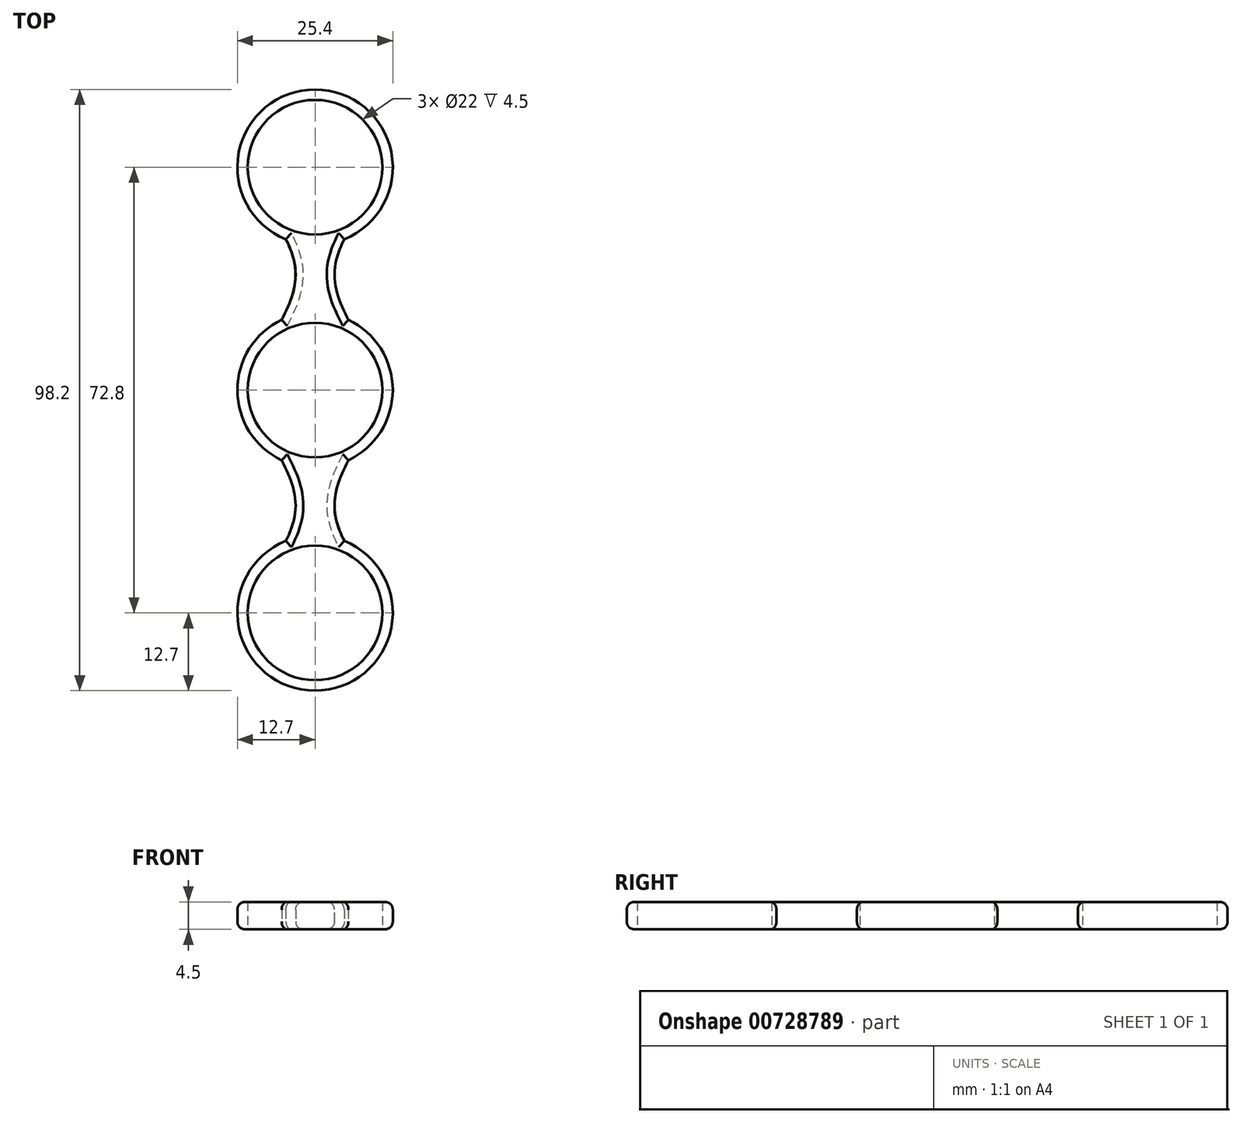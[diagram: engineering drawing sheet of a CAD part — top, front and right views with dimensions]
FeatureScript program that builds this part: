
annotation { "Feature Type Name" : "Feature", "Feature Type Description" : "" }
export const myFeature = defineFeature(function(context is Context, id is Id, definition is map)
    precondition{}
    {
        {
            var Q0;
            Q0=qCreatedBy(makeId("Top.planeOp"),FACE);
            var sketch = newSketch(context, id + "F0", { "sketchPlane" : qUnion([Q0])});
            skCircle(sketch, "E0", {"center": v(0, 0) * mm, "radius": 12.7 * mm});
            skCircle(sketch, "E1", {"center": v(0, 36.4) * mm, "radius": 11 * mm});
            skLineSegment(sketch, "E2", {"start": v(0, 25.4) * mm, "end": v(0, 12.7) * mm});
            skCircle(sketch, "E3", {"center": v(0, 0) * mm, "radius": 11 * mm});
            skCircle(sketch, "E4", {"center": v(0, -36.4) * mm, "radius": 11 * mm});
            skLineSegment(sketch, "E5", {"start": v(0, -12.7) * mm, "end": v(0, -25.4) * mm});
            skCircle(sketch, "E6", {"center": v(0, 36.4) * mm, "radius": 4 * mm});
            skCircle(sketch, "E7", {"center": v(0, -36.4) * mm, "radius": 4 * mm});
            skCircle(sketch, "E8", {"center": v(0, 0) * mm, "radius": 4 * mm});
            skCircle(sketch, "E9", {"center": v(0, 36.4) * mm, "radius": 12.7 * mm});
            skCircle(sketch, "E10", {"center": v(0, -36.4) * mm, "radius": 12.7 * mm});
            skFitSpline(sketch, "E11", {"points": [v(-12.7, 36.4) * mm, v(-12.7, 0) * mm], "startDerivative": vector(38.1, -52.05) * mm, "endDerivative": vector(-38.1, -57.15) * mm});
            skFitSpline(sketch, "E12", {"points": [v(12.7, 36.4) * mm, v(12.7, 0) * mm], "startDerivative": vector(-38.1, -52.05) * mm, "endDerivative": vector(38.1, -57.15) * mm});
            skFitSpline(sketch, "E13", {"points": [v(-12.7, 0) * mm, v(-12.7, -36.4) * mm], "startDerivative": vector(38.1, -57.15) * mm, "endDerivative": vector(-38.1, -52.05) * mm});
            skFitSpline(sketch, "E14", {"points": [v(12.7, 0) * mm, v(12.7, -36.4) * mm], "startDerivative": vector(-38.1, -57.15) * mm, "endDerivative": vector(38.1, -52.05) * mm});
            skSolve(sketch);
        }
        {
            var Q0;
            Q0 = qSketchRegion(id + "F0", true);
            extrude(context, id + "F1", {"entities" : qUnion([Q0]), "endBound" : BoundingType.SYMMETRIC, "depth" : 4.5 * mm, "offsetDistance" : 25.4 * mm});
        }
        {
            var Q0;
            Q0=makeQuery(id+"F1.opExtrude","CAP_EDGE",EDGE,{"disambiguationData":[OSD([sQuery(id+"F0.wireOp",EDGE,"E11")])],"isStart":false});
            var Q1;
            Q1=makeQuery(id+"F1.opExtrude","CAP_EDGE",EDGE,{"disambiguationData":[OSD([sQuery(id+"F0.wireOp",EDGE,"E14")])],"isStart":false});
            var Q2;
            Q2=makeQuery(id+"F1.opExtrude","CAP_EDGE",EDGE,{"disambiguationData":[OSD([sQuery(id+"F0.wireOp",EDGE,"E12")])],"isStart":false});
            var Q3;
            Q3=makeQuery(id+"F1.opExtrude","CAP_EDGE",EDGE,{"disambiguationData":[OSD([sQuery(id+"F0.wireOp",EDGE,"E13")])],"isStart":false});
            var Q4;
            Q4=makeQuery(id+"F1.opExtrude","CAP_EDGE",EDGE,{"disambiguationData":[OSD([sQuery(id+"F0.wireOp",EDGE,"E9")])],"isStart":false});
            var Q5;
            Q5=makeQuery(id+"F1.opExtrude","CAP_EDGE",EDGE,{"disambiguationData":[OSD([sQuery(id+"F0.wireOp",EDGE,"E10")])],"isStart":false});
            var Q6;
            {var subQ0=sQuery(id+"F0.wireOp",EDGE,"E13");var subQ1=sQuery(id+"F0.wireOp",EDGE,"E11");var subQ2=sQuery(id+"F0.wireOp",EDGE,"E0");Q6=makeQuery(id+"F1.opExtrude","CAP_EDGE",EDGE,{"disambiguationData":[OSD([subQ2]),TDD([makeQuery(id+"F0.imprint","IMPRINT",EDGE,{"disambiguationData":[TD([[makeQuery(id+"F0.imprint","INTERSECT",VERTEX,{"derivedFrom":[subQ2,subQ1]}),-1.0]])],"derivedFrom":subQ2}),makeQuery(id+"F0.imprint","IMPRINT",EDGE,{"disambiguationData":[TD([[makeQuery(id+"F0.imprint","INTERSECT",VERTEX,{"derivedFrom":[subQ2,subQ0]}),1.0]])],"derivedFrom":subQ2})])],"isStart":false});}
            var Q7;
            {var subQ0=sQuery(id+"F0.wireOp",EDGE,"E14");var subQ1=sQuery(id+"F0.wireOp",EDGE,"E12");var subQ2=sQuery(id+"F0.wireOp",EDGE,"E0");Q7=makeQuery(id+"F1.opExtrude","CAP_EDGE",EDGE,{"disambiguationData":[OSD([subQ2]),TDD([makeQuery(id+"F0.imprint","IMPRINT",EDGE,{"disambiguationData":[TD([[makeQuery(id+"F0.imprint","INTERSECT",VERTEX,{"derivedFrom":[subQ2,subQ1]}),1.0]])],"derivedFrom":subQ2}),makeQuery(id+"F0.imprint","IMPRINT",EDGE,{"disambiguationData":[TD([[makeQuery(id+"F0.imprint","INTERSECT",VERTEX,{"derivedFrom":[subQ2,subQ0]}),-1.0]])],"derivedFrom":subQ2})])],"isStart":false});}
            var Q8;
            Q8=makeQuery(id+"F1.opExtrude","CAP_EDGE",EDGE,{"disambiguationData":[OSD([sQuery(id+"F0.wireOp",EDGE,"E10")])],"isStart":true});
            var Q9;
            Q9=makeQuery(id+"F1.opExtrude","CAP_EDGE",EDGE,{"disambiguationData":[OSD([sQuery(id+"F0.wireOp",EDGE,"E14")])],"isStart":true});
            var Q10;
            {var subQ0=sQuery(id+"F0.wireOp",EDGE,"E14");var subQ1=sQuery(id+"F0.wireOp",EDGE,"E12");var subQ2=sQuery(id+"F0.wireOp",EDGE,"E0");Q10=makeQuery(id+"F1.opExtrude","CAP_EDGE",EDGE,{"disambiguationData":[OSD([subQ2]),TDD([makeQuery(id+"F0.imprint","IMPRINT",EDGE,{"disambiguationData":[TD([[makeQuery(id+"F0.imprint","INTERSECT",VERTEX,{"derivedFrom":[subQ2,subQ1]}),1.0]])],"derivedFrom":subQ2}),makeQuery(id+"F0.imprint","IMPRINT",EDGE,{"disambiguationData":[TD([[makeQuery(id+"F0.imprint","INTERSECT",VERTEX,{"derivedFrom":[subQ2,subQ0]}),-1.0]])],"derivedFrom":subQ2})])],"isStart":true});}
            var Q11;
            Q11=makeQuery(id+"F1.opExtrude","CAP_EDGE",EDGE,{"disambiguationData":[OSD([sQuery(id+"F0.wireOp",EDGE,"E9")])],"isStart":true});
            var Q12;
            {var subQ0=sQuery(id+"F0.wireOp",EDGE,"E13");var subQ1=sQuery(id+"F0.wireOp",EDGE,"E11");var subQ2=sQuery(id+"F0.wireOp",EDGE,"E0");Q12=makeQuery(id+"F1.opExtrude","CAP_EDGE",EDGE,{"disambiguationData":[OSD([subQ2]),TDD([makeQuery(id+"F0.imprint","IMPRINT",EDGE,{"disambiguationData":[TD([[makeQuery(id+"F0.imprint","INTERSECT",VERTEX,{"derivedFrom":[subQ2,subQ1]}),-1.0]])],"derivedFrom":subQ2}),makeQuery(id+"F0.imprint","IMPRINT",EDGE,{"disambiguationData":[TD([[makeQuery(id+"F0.imprint","INTERSECT",VERTEX,{"derivedFrom":[subQ2,subQ0]}),1.0]])],"derivedFrom":subQ2})])],"isStart":true});}
            var Q13;
            Q13=makeQuery(id+"F1.opExtrude","CAP_EDGE",EDGE,{"disambiguationData":[OSD([sQuery(id+"F0.wireOp",EDGE,"E11")])],"isStart":true});
            var Q14;
            Q14=makeQuery(id+"F1.opExtrude","CAP_EDGE",EDGE,{"disambiguationData":[OSD([sQuery(id+"F0.wireOp",EDGE,"E13")])],"isStart":true});
            var Q15;
            Q15=makeQuery(id+"F1.opExtrude","CAP_EDGE",EDGE,{"disambiguationData":[OSD([sQuery(id+"F0.wireOp",EDGE,"E12")])],"isStart":true});
            fillet(context, id + "F2", {"entities" : qUnion([Q0, Q1, Q2, Q3, Q4, Q5, Q6, Q7, Q8, Q9, Q10, Q11, Q12, Q13, Q14, Q15]), "radius" : 1.27 * mm, "tangentPropagation" : true, "allowEdgeOverflow" : false});
        }
    });
